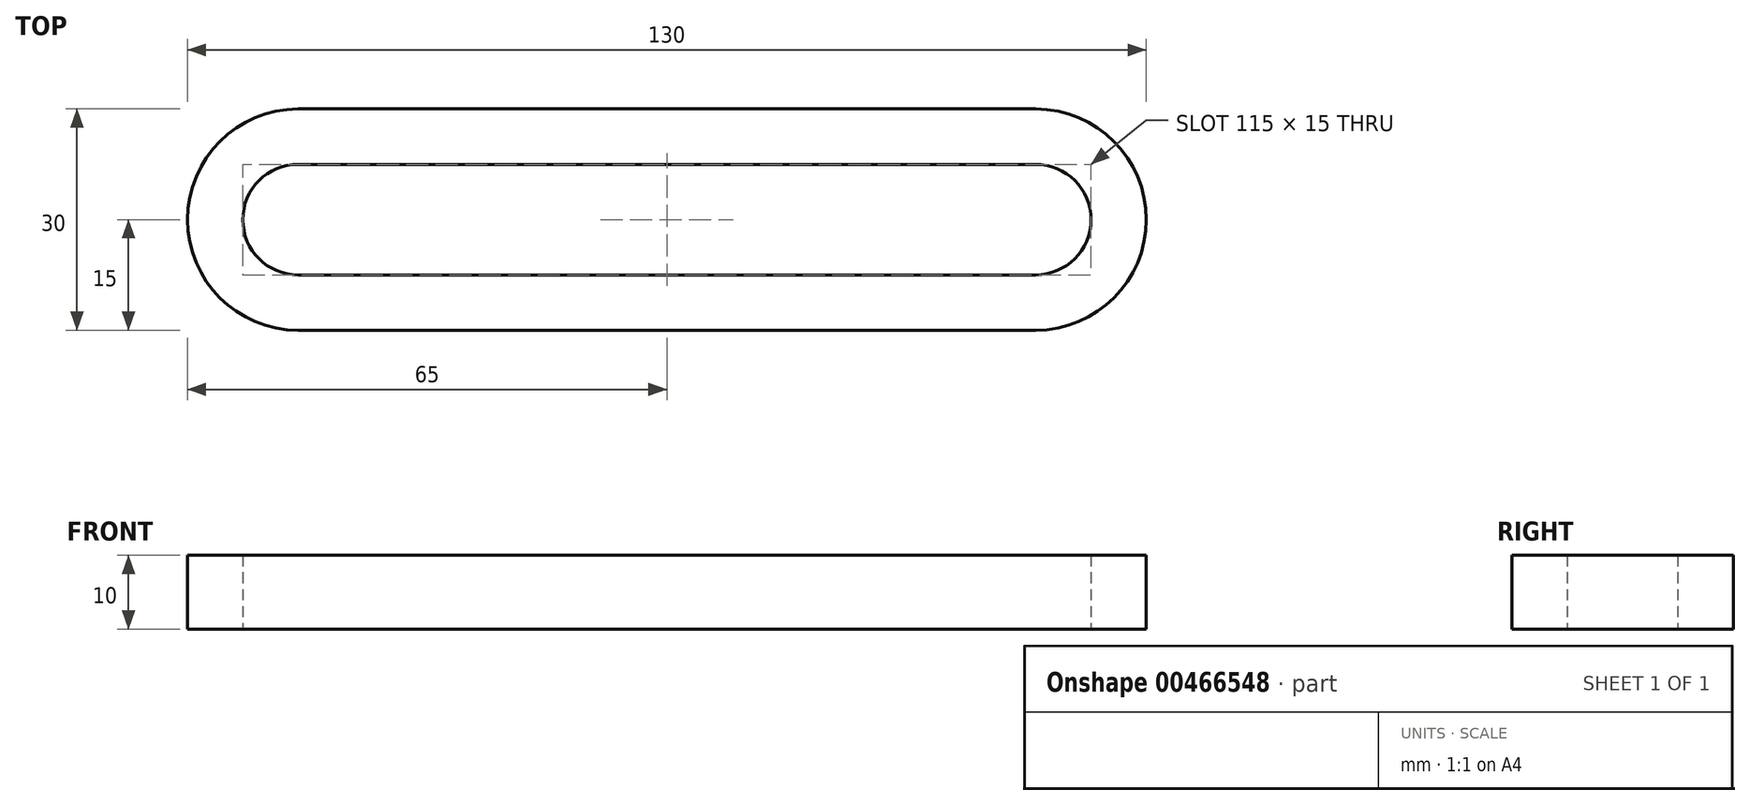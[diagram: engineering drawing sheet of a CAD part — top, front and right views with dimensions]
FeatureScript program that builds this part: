
annotation { "Feature Type Name" : "Feature", "Feature Type Description" : "" }
export const myFeature = defineFeature(function(context is Context, id is Id, definition is map)
    precondition{}
    {
        {
            var Q0;
            Q0=qCreatedBy(makeId("Top.planeOp"),FACE);
            var sketch = newSketch(context, id + "F0", { "sketchPlane" : qUnion([Q0])});
            skArc(sketch, "E0", {"start": v(50, -15) * mm, "mid": v(65, 0) * mm, "end": v(50, 15) * mm});
            skArc(sketch, "E1.MirrorC", {"start": v(-50, -15) * mm, "mid": v(-65, 0) * mm, "end": v(-50, 15) * mm});
            skLineSegment(sketch, "E2", {"start": v(-50, 15) * mm, "end": v(50, 15) * mm});
            skLineSegment(sketch, "E3", {"start": v(-50, -15) * mm, "end": v(50, -15) * mm});
            skArc(sketch, "E4", {"start": v(-50, 7.5) * mm, "mid": v(-57.5, 0) * mm, "end": v(-50, -7.5) * mm});
            skArc(sketch, "E5", {"start": v(50, -7.5) * mm, "mid": v(57.5, 0) * mm, "end": v(50, 7.5) * mm});
            skLineSegment(sketch, "E6", {"start": v(-50, 7.5) * mm, "end": v(50, 7.5) * mm});
            skLineSegment(sketch, "E7", {"start": v(-50, -7.5) * mm, "end": v(50, -7.5) * mm});
            skSolve(sketch);
        }
        {
            var Q0;
            Q0=makeQuery(id+"F0.imprint","IMPRINT",FACE,{"disambiguationData":[TD([[makeQuery(id+"F0.imprint","IMPRINT",EDGE,{"derivedFrom":sQuery(id+"F0.wireOp",EDGE,"E0")}),1.0]])]});
            extrude(context, id + "F1", {"entities" : qUnion([Q0]), "depth" : 10 * mm});
        }
    });
